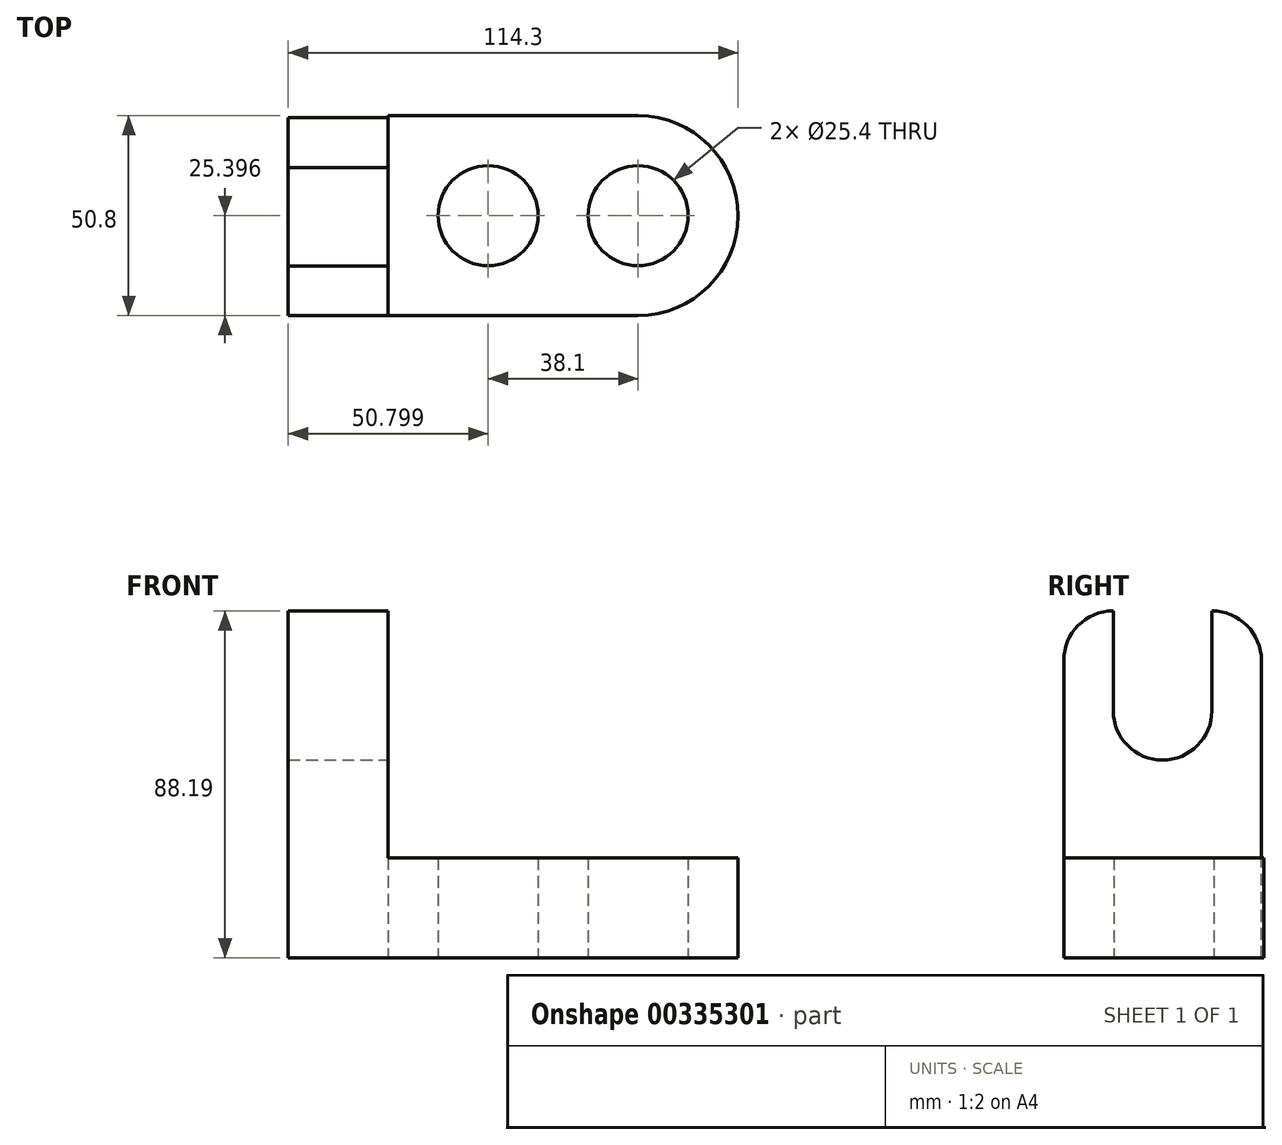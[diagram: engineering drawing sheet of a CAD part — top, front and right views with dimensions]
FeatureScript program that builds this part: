
annotation { "Feature Type Name" : "Feature", "Feature Type Description" : "" }
export const myFeature = defineFeature(function(context is Context, id is Id, definition is map)
    precondition{}
    {
        {
            var Q0;
            Q0=qCreatedBy(makeId("Top.planeOp"),FACE);
            var sketch = newSketch(context, id + "F0", { "sketchPlane" : qUnion([Q0])});
            skLineSegment(sketch, "E0.bottom", {"start": v(-33.57, 21.84) * mm, "end": v(29.93, 21.84) * mm});
            skLineSegment(sketch, "E0.top", {"start": v(-33.57, -28.96) * mm, "end": v(29.93, -28.96) * mm});
            skLineSegment(sketch, "E0.left", {"start": v(-33.57, 21.84) * mm, "end": v(-33.57, -28.96) * mm});
            skArc(sketch, "E1", {"start": v(29.93, -28.96) * mm, "mid": v(55.33, -3.56) * mm, "end": v(29.93, 21.84) * mm});
            skCircle(sketch, "E2", {"center": v(-8.17, -3.56) * mm, "radius": 12.7 * mm});
            skPoint(sketch, "E2.centerSnap0", {"position": v(-33.57, -3.56) * mm});
            skCircle(sketch, "E3", {"center": v(29.93, -3.56) * mm, "radius": 12.7 * mm});
            skSolve(sketch);
        }
        {
            var Q0;
            Q0=makeQuery(id+"F0.imprint","IMPRINT",FACE,{"disambiguationData":[TD([[makeQuery(id+"F0.imprint","IMPRINT",EDGE,{"derivedFrom":sQuery(id+"F0.wireOp",EDGE,"E0.bottom")}),-1.0]])]});
            extrude(context, id + "F1", {"entities" : qUnion([Q0]), "depth" : 25.4 * mm});
        }
        {
            var Q0;
            Q0=makeQuery(id+"F1.opExtrude","SWEPT_FACE",FACE,{"disambiguationData":[OSD([sQuery(id+"F0.wireOp",EDGE,"E0.left")])]});
            var sketch = newSketch(context, id + "F2", { "sketchPlane" : qUnion([Q0])});
            skLineSegment(sketch, "E4.bottom", {"start": v(28.96, 0) * mm, "end": v(-21.28, 0) * mm});
            skLineSegment(sketch, "E4.left", {"start": v(28.96, 0) * mm, "end": v(28.96, 62.79) * mm});
            skLineSegment(sketch, "E4.right", {"start": v(-21.28, 0) * mm, "end": v(-21.28, 62.79) * mm});
            skArc(sketch, "E5", {"start": v(-8.7, 62.79) * mm, "mid": v(3.84, 50.26) * mm, "end": v(16.37, 62.79) * mm});
            skLineSegment(sketch, "E6", {"start": v(-8.7, 62.79) * mm, "end": v(-8.7, 88.19) * mm});
            skLineSegment(sketch, "E7", {"start": v(-8.58, 88.19) * mm, "end": v(-8.7, 88.19) * mm});
            skLineSegment(sketch, "E8", {"start": v(-21.28, 75.49) * mm, "end": v(-21.28, 62.79) * mm});
            skLineSegment(sketch, "E9", {"start": v(16.37, 62.79) * mm, "end": v(16.37, 88.19) * mm});
            skLineSegment(sketch, "E10", {"start": v(16.26, 88.19) * mm, "end": v(16.37, 88.19) * mm});
            skLineSegment(sketch, "E11", {"start": v(28.96, 75.49) * mm, "end": v(28.96, 62.79) * mm});
            skPoint(sketch, "E12.visualSharp", {"position": v(-21.28, 88.19) * mm});
            skArc(sketch, "E12.filletArc", {"start": v(-8.58, 88.19) * mm, "mid": v(-17.56, 84.47) * mm, "end": v(-21.28, 75.49) * mm});
            skPoint(sketch, "E13.visualSharp", {"position": v(28.96, 88.19) * mm});
            skArc(sketch, "E13.filletArc", {"start": v(28.96, 75.49) * mm, "mid": v(25.24, 84.47) * mm, "end": v(16.26, 88.19) * mm});
            skSolve(sketch);
        }
        {
            var Q0;
            {var subQ0=sQuery(id+"F2.wireOp",EDGE,"E5");Q0=makeQuery(id+"F2.imprint","IMPRINT",FACE,{"disambiguationData":[TD([[makeQuery(id+"F2.imprint","IMPRINT",EDGE,{"derivedFrom":subQ0}),-1.0]])]});}
            var Q1;
            {var subQ0=sQuery(id+"F2.wireOp",EDGE,"E4.bottom");Q1=makeQuery(id+"F2.imprint","IMPRINT",FACE,{"disambiguationData":[TD([[makeQuery(id+"F2.imprint","IMPRINT",EDGE,{"derivedFrom":subQ0}),1.0]])]});}
            extrude(context, id + "F3", {"entities" : qUnion([Q0, Q1]), "operationType" : NewBodyOperationType.ADD, "depth" : 25.4 * mm});
        }
    });
